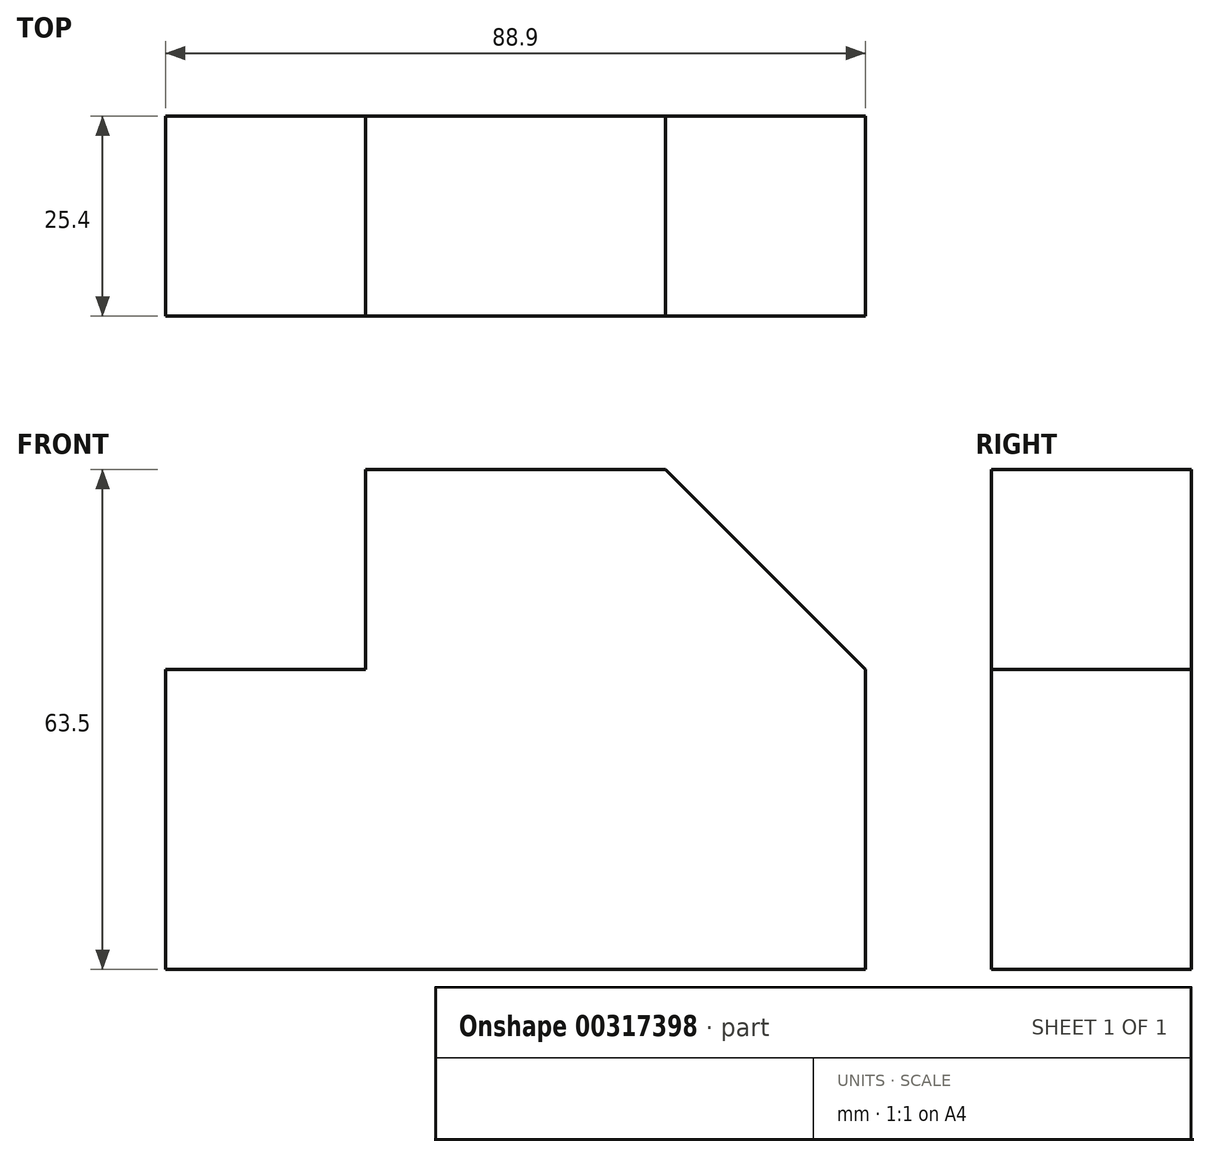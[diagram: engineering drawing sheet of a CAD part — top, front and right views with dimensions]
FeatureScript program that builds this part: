
annotation { "Feature Type Name" : "Feature", "Feature Type Description" : "" }
export const myFeature = defineFeature(function(context is Context, id is Id, definition is map)
    precondition{}
    {
        {
            var Q0;
            Q0=qCreatedBy(makeId("Front.planeOp"),FACE);
            var sketch = newSketch(context, id + "F0", { "sketchPlane" : qUnion([Q0])});
            skLineSegment(sketch, "E0", {"start": v(-62.42, -38.1) * mm, "end": v(26.48, -38.1) * mm});
            skLineSegment(sketch, "E1", {"start": v(26.48, -38.1) * mm, "end": v(26.48, 0) * mm});
            skLineSegment(sketch, "E2", {"start": v(26.48, 0) * mm, "end": v(1.08, 25.4) * mm});
            skLineSegment(sketch, "E3", {"start": v(-62.42, -38.1) * mm, "end": v(-62.42, 0) * mm});
            skLineSegment(sketch, "E4", {"start": v(-62.42, 0) * mm, "end": v(-37.02, 0) * mm});
            skLineSegment(sketch, "E5", {"start": v(-37.02, 0) * mm, "end": v(-37.02, 25.4) * mm});
            skLineSegment(sketch, "E6", {"start": v(-37.02, 25.4) * mm, "end": v(1.08, 25.4) * mm});
            skSolve(sketch);
        }
        {
            var Q0;
            Q0=makeQuery(id+"F0.imprint","IMPRINT",FACE,{"disambiguationData":[TD([[makeQuery(id+"F0.imprint","IMPRINT",EDGE,{"derivedFrom":sQuery(id+"F0.wireOp",EDGE,"E0")}),1.0]])]});
            extrude(context, id + "F1", {"entities" : qUnion([Q0]), "depth" : 25.4 * mm});
        }
    });
